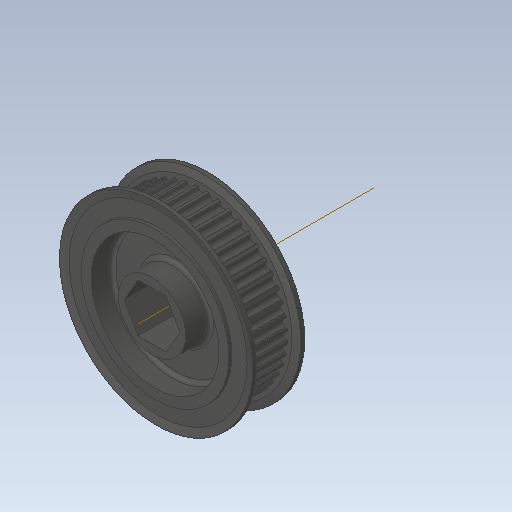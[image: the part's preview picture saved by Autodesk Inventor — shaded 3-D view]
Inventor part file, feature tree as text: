
AUTODESK INVENTOR PART (.ipt)
format: ipt  version: 2020 (Build 240168000, 168)  size: 566,272 bytes
history: native  units: in
note: dims shown in document units (in); Inventor stores cm internally (conversion verified against a paired STEP export)
features: other x1, fillet x1
ambient origin geometry x8: Origin, YZ Plane, XZ Plane, XY Plane, X Axis, Y Axis, Z Axis, Center Point
bodies: Solid1 (feature_tree)
feature tree (2):
  other  "Work Axis1"
  fillet  "Fillet1"  [1 undecoded]
note: 1 required parameter value undecoded (feature->parameter linkage not recoverable at this tier; creation-order binding heuristic only, values carry confidence <= 0.55)
